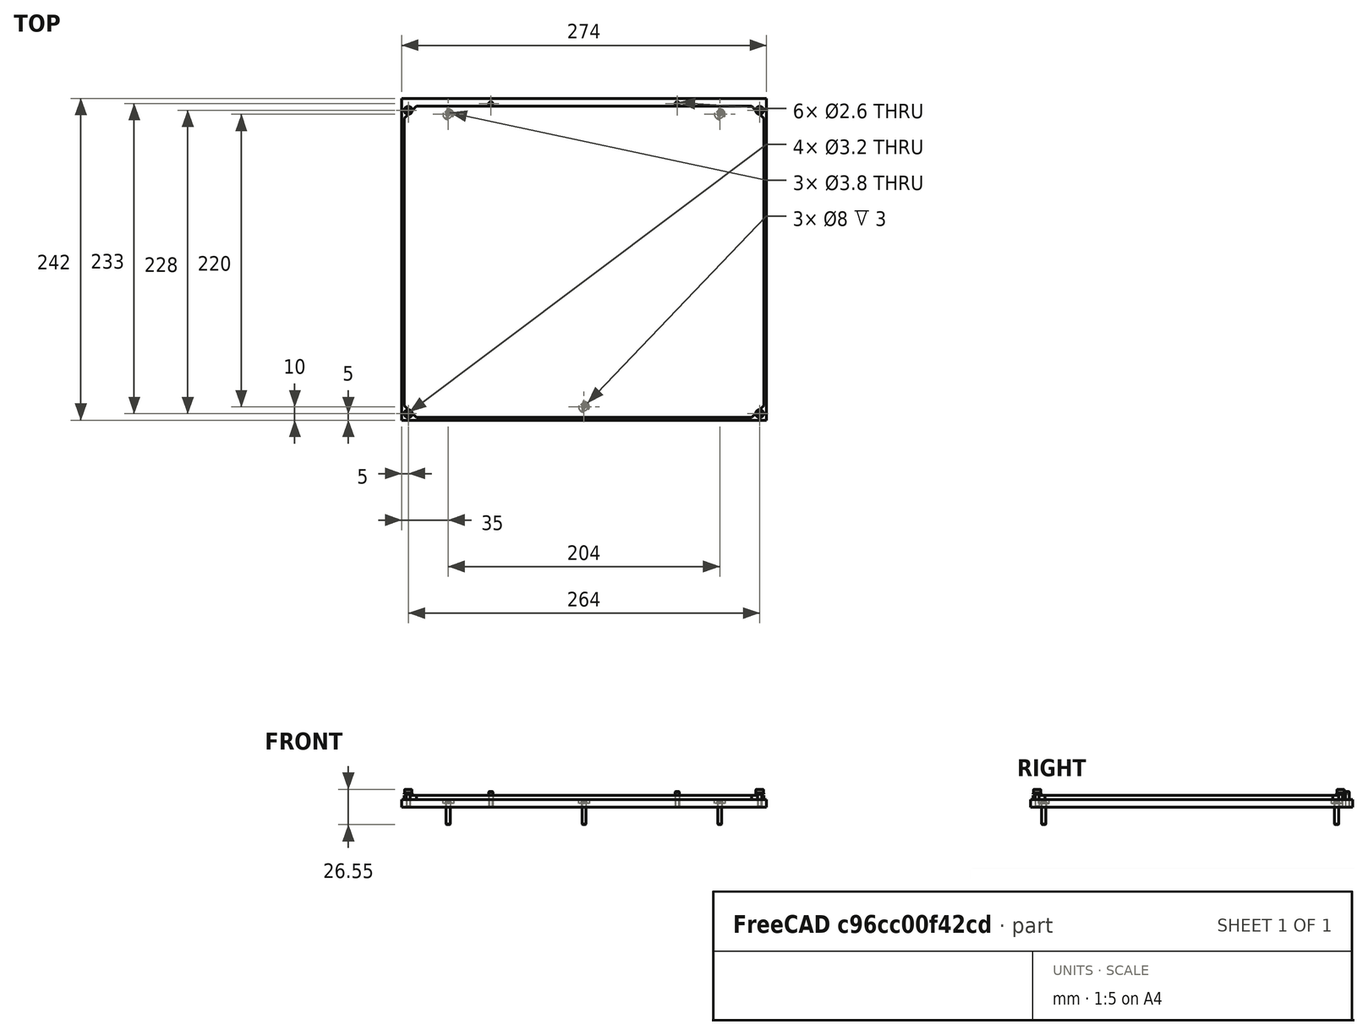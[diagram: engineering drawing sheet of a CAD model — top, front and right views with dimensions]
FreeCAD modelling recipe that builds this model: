
FCSTD DOCUMENT  (FreeCAD 0.19R24291 (Git))
Label: 250-glass-bed-assembly
License: Other
LicenseURL: GPL3
objects: Part::FeaturePython×13, Part::Feature×2, App::Part×1
note: 15 computed .brp shape members not serialized (recipe doc carries the construction recipe); baked Part::Feature solids carry a one-line shape summary decoded from their .brp

FEATURE [Part::Feature] Body003001  label="250-glass-plate"
  Placement = pos=(0,0,-8) rot=(0,0,1;0rad)
  shape: bbox 270 x 234 x 3 mm, 10 faces (baked)
FEATURE [Part::Feature] Body002001  label="250-aluminum-plate"
  Placement = pos=(0,0,-14) rot=(0,0,1;0rad)
  shape: bbox 274 x 242 x 6 mm, 21 faces (baked)
FEATURE [Part::FeaturePython] Screw  label="M3x16-Screw"  # Fasteners workbench fastener (typed FeaturePython)
  Placement = pos=(-102,110,-11) rot=(0,0,1;0rad)
  baseObject = -> Body002001 [Edge34]
  diameter = 1
  invert = true
  length = 5
  lengthCustom = 16
  matchOuter = true
  offset = 0
  thread = false
  type = 40
FEATURE [Part::FeaturePython] Screw001  label="M3x16-Screw001"  # Fasteners workbench fastener (typed FeaturePython)
  Placement = pos=(102,110,-11) rot=(0,0,1;0rad)
  baseObject = -> Body002001 [Edge32]
  diameter = 1
  invert = true
  length = 5
  lengthCustom = 16
  matchOuter = true
  offset = 0
  thread = false
  type = 40
FEATURE [Part::FeaturePython] Screw002  label="M3x16-Screw002"  # Fasteners workbench fastener (typed FeaturePython)
  Placement = pos=(0,-110,-11) rot=(0,0,1;0rad)
  baseObject = -> Body002001 [Edge36]
  diameter = 1
  invert = true
  length = 5
  lengthCustom = 16
  matchOuter = true
  offset = 0
  thread = false
  type = 40
FEATURE [Part::FeaturePython] Screw003  label="M3x12-Screw"  # Fasteners workbench fastener (typed FeaturePython)
  Placement = pos=(-70,118,-2) rot=(0,0,1;0rad)
  baseObject = -> Body002001 [Edge28]
  diameter = 6
  invert = false
  length = 7
  lengthCustom = 12
  matchOuter = true
  offset = 6
  thread = false
  type = 30
FEATURE [Part::FeaturePython] Screw004  label="M3x12-Screw001"  # Fasteners workbench fastener (typed FeaturePython)
  Placement = pos=(70,118,-2) rot=(0,0,1;0rad)
  baseObject = -> Body002001 [Edge27]
  diameter = 6
  invert = false
  length = 7
  lengthCustom = 12
  matchOuter = true
  offset = 6
  thread = false
  type = 30
FEATURE [Part::FeaturePython] Washer  label="M3-silicon-Washer"  # Fasteners workbench fastener (typed FeaturePython)
  Placement = pos=(-132,113,-4) rot=(0,0,1;0rad)
  baseObject = -> Body002001 [Edge30]
  diameter = 4
  invert = false
  matchOuter = true
  offset = 4
  type = 5
FEATURE [Part::FeaturePython] Washer001  label="M3-silicon-Washer001"  # Fasteners workbench fastener (typed FeaturePython)
  Placement = pos=(132,113,-4) rot=(0,0,1;0rad)
  baseObject = -> Body002001 [Edge25]
  diameter = 4
  invert = false
  matchOuter = true
  offset = 4
  type = 5
FEATURE [Part::FeaturePython] Washer002  label="M3-silicon-Washer002"  # Fasteners workbench fastener (typed FeaturePython)
  Placement = pos=(132,-115,-4) rot=(0,0,1;0rad)
  baseObject = -> Body002001 [Edge22]
  diameter = 4
  invert = false
  matchOuter = true
  offset = 4
  type = 5
FEATURE [Part::FeaturePython] Washer003  label="M3-silicon-Washer003"  # Fasteners workbench fastener (typed FeaturePython)
  Placement = pos=(-132,-115,-4) rot=(0,0,1;0rad)
  baseObject = -> Body002001 [Edge24]
  diameter = 4
  invert = false
  matchOuter = true
  offset = 4
  type = 5
FEATURE [Part::FeaturePython] Screw005  label="M3x10-low-head-Screw"  # Fasteners workbench fastener (typed FeaturePython)
  Placement = pos=(-132,113,-3.45) rot=(0,0,1;0rad)
  baseObject = -> Washer [Edge1]
  diameter = 4
  invert = false
  length = 3
  lengthCustom = 10
  matchOuter = true
  offset = 0
  thread = false
  type = 34
FEATURE [Part::FeaturePython] Screw006  label="M3x10-low-head-Screw001"  # Fasteners workbench fastener (typed FeaturePython)
  Placement = pos=(-132,-115,-3.45) rot=(0,0,1;0rad)
  baseObject = -> Washer003 [Edge1]
  diameter = 4
  invert = false
  length = 3
  lengthCustom = 10
  matchOuter = true
  offset = 0
  thread = false
  type = 34
FEATURE [Part::FeaturePython] Screw007  label="M3x10-low-head-Screw002"  # Fasteners workbench fastener (typed FeaturePython)
  Placement = pos=(132,-115,-3.45) rot=(0,0,1;0rad)
  baseObject = -> Washer002 [Edge1]
  diameter = 4
  invert = false
  length = 3
  lengthCustom = 10
  matchOuter = true
  offset = 0
  thread = false
  type = 34
FEATURE [Part::FeaturePython] Screw008  label="M3x10-low-head-Screw003"  # Fasteners workbench fastener (typed FeaturePython)
  Placement = pos=(132,113,-3.45) rot=(0,0,1;0rad)
  baseObject = -> Washer001 [Edge1]
  diameter = 4
  invert = false
  length = 3
  lengthCustom = 10
  matchOuter = true
  offset = 0
  thread = false
  type = 34
FEATURE [App::Part] Part  label="250-glass"
  Group = -> [Body003001,Body002001,Screw,Screw001,Screw002,Screw003,Screw004,Washer,Washer001,Washer002,Washer003,Screw005,Screw006,Screw007,Screw008]
  Origin = -> Origin
